# Revit family: NBS_Allermuir_OffcChrs_Famiglia-en-us_MidBack
name_source: partatom
category: Furniture
revit_build: Autodesk Revit 2016 (Build: 20151007_0715(x64)
units: mm (PartAtom-declared; Revit-internal decimal feet)

## family parameters
Always vertical = Yes
Cut with Voids When Loaded = No
Room Calculation Point = No
Shared = No
Work Plane-Based = No

## types (4) — shared parameters
AssetType = Moveable
Category = Pr_40_50_12_57:Office chairs
CodePerformance = AMIS/BIFMA X5.1: 2011
DurationUnit = year
EnvironmentalProductDeclaration = http://www.thesenatorgroup.com
ExpectedLife = 10
FrameMountingMaterial = NBS_Concept
IfcExportAs = IfcFurnitureType
IfcExportType = CHAIR
IsBuiltIn = No
ManufacturerName = Allermuir
ManufacturerURL = http://www.thesenatorgroup.com
ModelReference = Famiglia mid
NBSCertification = www.nationalbimlibrary.com/cert/aqurbcen
NBSDescription = Office chairs
NBSReference = 45-35-20/330
OmniClassCode = 22-12 52 23
OmniClassTitle = Office Seating
OmniClassVersion = Table 22 2012-05-16
ProductInformation = http://www.thesenatorgroup.com
SeatBaseMaterial = NBS_Concept
SeatFrameMaterial = NBS_Concept
SeatingSeatMaterial = NBS_Concept
SeatsAndBacksFinish = Fully upholstered
SeatsAndBacksFinishOptions = Decorative railroad stitch detail to perimeter seam, two-tone upholstery
SeatsAndBacksMaterial = Molded foam
StandardsDurability = AMIS/BIFMA X5.1: 2011
StandardsSafetyRequirements = AMIS/BIFMA X5.1: 2011
Status = UNSET
Uniclass2015Code = Pr_40_50_12_57
Uniclass2015Title = Office chairs
Uniclass2015Version = Products v1.9
Version = 1
WarrantyDescription = Allermuir warrant that its manufactured products are free from manufacturing defects in materials or workmanship for a period of ten years
WarrantyDurationParts = 10
WarrantyDurationUnit = year
WorkTableFrameMaterial = NBS_Concept
WorkTableMaterial = NBS_Concept

## per-type parameters (varying)
| type | BIMObjectName | Description | Features | FrameColour | FrameColourOptions | FrameFinish | FrameFinishOptions | FrameMaterials | HasWorkTable | HighestSeatingHeight | IntegralAccessories | LowestSeatingHeight | Name | NominalDepth | NominalHeight | NominalLength | NominalWidth | OfficeChairBase | SeatingHeight | SeatsAndBacksColourOptions | Size |
| FMG202 | NBS_Allermuir_OfficeChairs_Famiglia_FMG202-US | Mid back on a 4 leg frame | Molded foam construction, fully upholstered, tubular steel frame with wire supports finished in polished chrome, plastic glides, tubular Steel frame with wire supports available in slate grey powder coat, plastic glides with felt | Chrome | Slate grey | Polished | Available in slate grey powder coat | Tubular steel | No | 0 " | Plastic glides | 0 " | OfficeChairs_Famiglia_FMG202-US_Allermuir | 26 " | 39 " | 27 " | 26 " | NBS_Allermuir_OffcChrs_Famiglia_4LegFrameHigh | 18 " | Black, White, Red, Light Grey, Dark Grey, Cream | 26.25 x 38.5 x 26.5" |
| FMG206 | NBS_Allermuir_OfficeChairs_Famiglia_FMG206-US | Mid back on a 5 star base | Molded foam construction, fully upholstered, 5 star polished aluminum base, static yoke - swivel only, swivel column in anthracite, 2.5" hard wheel castors |  |  | Swivel column in anthracite, base polished aluminum |  | Aluminum | No | 22 " | 2.5" hard wheel castors | 17 " | OfficeChairs_Famiglia_FMG206-US_Allermuir | 26 " | 42 " | 25 " | 26 " | NBS_Allermuir_OffcChrs_Famiglia_5StarBase | 19 " | Black, White, Red, Light Grey, Dark Grey, Cream | 25.5 x 42 x 24.5" |
| FMG207 | NBS_Allermuir_OfficeChairs_Famiglia_FMG207-US | Mid back on a 5 star base with tablet | Molded foam construction, fully upholstered, 5 star polished aluminum base, static yoke - swivel only, swivel column in anthracite, soft touch PU orbital, fold down work surface in anthracite, 2.5" hard wheel castors |  |  | Swivel column in anthracite, base polished aluminum |  | Aluminum | Yes | 0 " | 2.5" hard wheel castors, soft touch PU orbital fold down work surface in anthracite | 0 " | OfficeChairs_Famiglia_FMG207-US_Allermuir | 25 " | 39 " | 26 " | 25 " | NBS_Allermuir_OffcChrs_Famiglia_5StarBase | 19 " | Colors: Black, White, Red, Light Grey, Dark Grey, Cream | 24.5 x 38.5 x 26.25" |
| FMG203 | NBS_Allermuir_OfficeChairs_Famiglia_FMG203-US | Mid back with wood legs | Molded foam construction, fully upholstered, aluminum leg connector frame finished in slate grey powder coat, solid Ash legs with a clear finish, plastic glides, solid ash legs can be stained or color washed, plastic glides with felt |  | Can be stained or color washed | Clear finish | Can be stained or color washed | Ash | No | 0 " | Plastic glides, aluminum leg connector frame finished in slate grey powder coat | 0 " | OfficeChairs_Famiglia_FMG203-US_Allermuir | 26 " | 39 " | 27 " | 26 " | NBS_Allermuir_OffcChrs_Famiglia_WoodLegs | 19 " | Black, White, Red, Light Grey, Dark Grey, Cream | 26.25 x 39.25 x 26.5" |

note: column(s) folded — value = type name in every type: ModelNumber

## geometry (parser evidence)
native form markers: Sweep x16
no freeform markers — native parametric forms only
